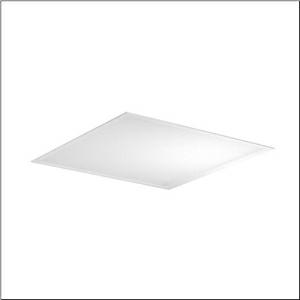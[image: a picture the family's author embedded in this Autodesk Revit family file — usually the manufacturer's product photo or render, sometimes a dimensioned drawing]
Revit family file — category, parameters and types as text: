
# Revit family: apollon_21_square_51mq12wd2m14
name_source: partatom
category: Lighting Fixtures
units: mm (PartAtom-declared; Revit-internal decimal feet)

## family parameters
Cut with Voids When Loaded = No
Host = Face
Light Source = No
Part Type = Normal
Room Calculation Point = No
Round Connector Dimension = Use Diameter
Shared = No

## types (1)
- --- (1 x LED, 4200 lm, 26 W, 4000K)
    Apparent Load = 26 VA
    CIE Flux Codes = 60 87 97 100 100
    Color Rendering = 80
    Color Temperature = 4000K
    Default Elevation = 1800 mm
    Description = Apollon 21 square, office luminaire, primary optical cover: micro prismatic cover, of PMMA, CAT 2 (L<= 3000cd/m²), light emission: direct distribution, primary light characteristic: symmetric, installation type: lay-in mounting, LED, rated luminous flux: 4.200lm, luminous efficacy: 162lm/W, light colour: 830/840, colour temperature: 3000/4000K, control gear: DALI 2, Multilumen, with terminal, 5-pole, mains connection: 220..240V, AC/DC, 0/50..60Hz, rated input power: 26W, housing, of aluminium, coated, traffic white (RAL 9016), module: M600, length: 595mm, width: 595mm, height: 55mm, recess depth: 180mm, housing upper side, of sheet steel, galvanised, protection rating (complete): IP20, protection rating (lamp compartment, on room side): IP50, insulation class (complete): insulation class II (safety insulation), certification: CE, ENEC, impact resistance: IK03, permissible operating ambient temperature: -20..+45°C, permissible storage temperature: -40..+80°C, standard: EN 60598-2-22, packaging unit: 1 piece
    Height = 0 mm  [stored 0 ft]
    Lamp = 1 x LED
    Lamp Light Flux = 4200 lm
    Lamp Power = 26 W
    Lamp count = 1
    Length = 595 mm
    Luminous efficacy = 162 lm/W
    Manufacturer = Siteco
    ModVariant = No
    Model = 51MQ12WD2M14
    Mounting Place = Ceiling
    Mounting Type = Recessed
    Number of Poles = 1
    OnlyDefault = Yes
    Power Factor = 1
    Product Name = Apollon 21 square
    Product group = office luminaire | ceiling recessed
    ProductGroupID = 401
    Protection Class = Protection class II
    Protection Degree = IP 20
    RLX_Detail_Level = 1
    RLX_Emergency_Light_Flux = 0 lm
    RLX_Emergency_Type = 0
    RLX_Emergency_Type_DB = No
    RlxData = <blob elided: 12757 chars, md5=660a6adb>
    Socket = socket
    Standby Power = 0 W
    System Light Flux = 4200 lm
    System Power = 26 W
    Type Comments = factory setting
    Type Image = l_1291049.jpg
    URL = http://relux.com
    VarID = @adj_068436
    Voltage = 0 V
    Weight = 0.00 kg
    Width = 595 mm

note: [stored X ft] marks values corroborated as IEEE doubles in the binary element streams (Revit-internal decimal feet)

## geometry (parser evidence)
native form markers: Sweep x10
no freeform markers — native parametric forms only
